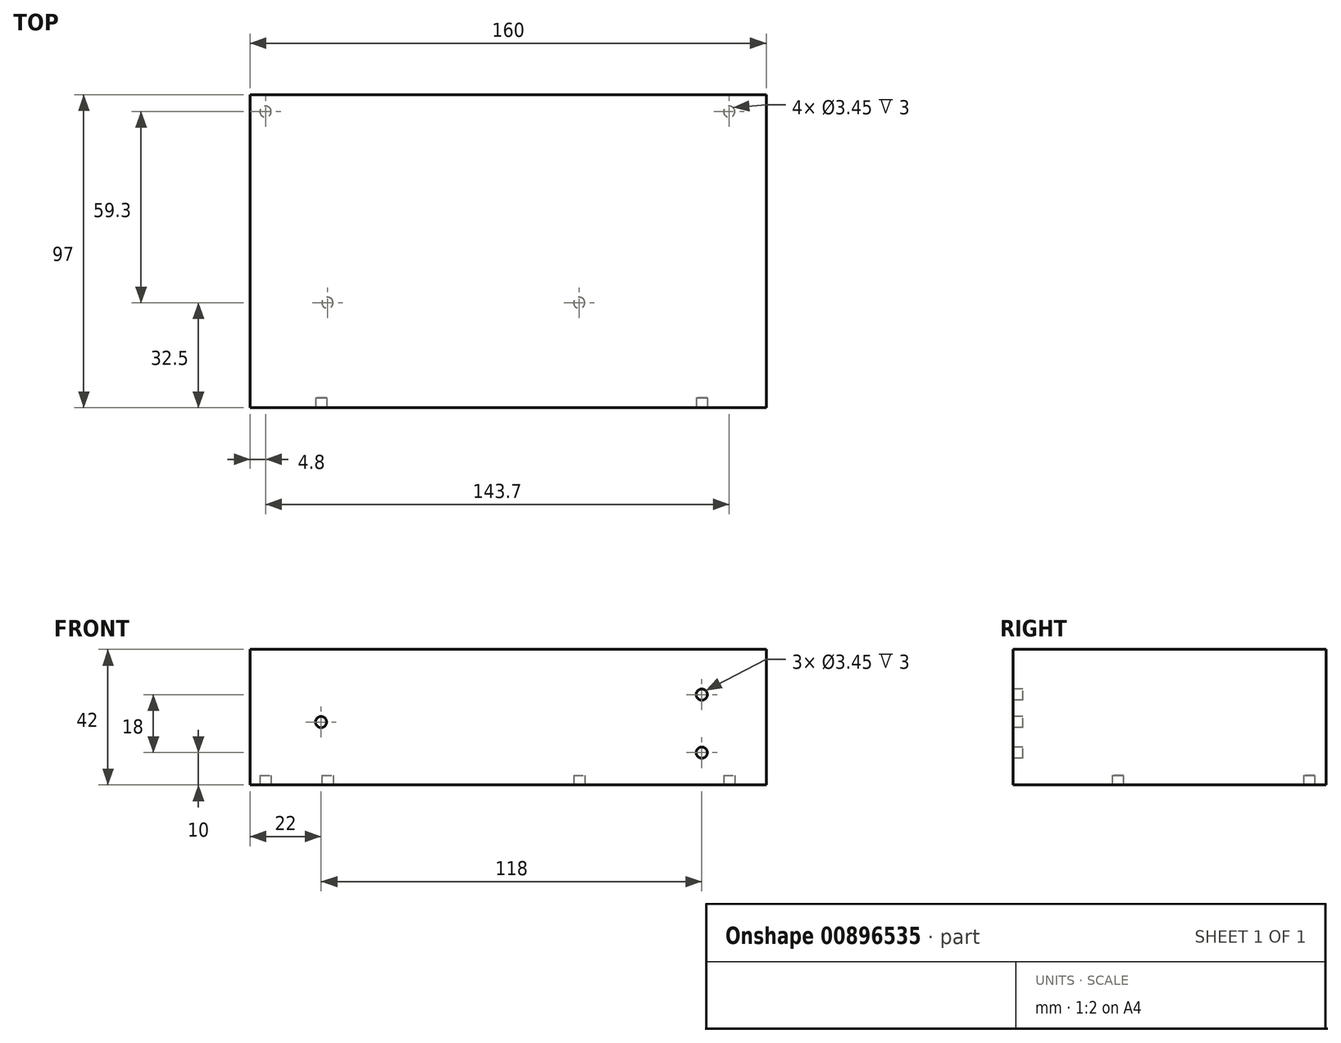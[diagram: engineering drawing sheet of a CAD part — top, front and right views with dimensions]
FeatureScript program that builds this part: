
annotation { "Feature Type Name" : "Feature", "Feature Type Description" : "" }
export const myFeature = defineFeature(function(context is Context, id is Id, definition is map)
    precondition{}
    {
        {
            var Q0;
            Q0=qCreatedBy(makeId("Top.planeOp"),FACE);
            var sketch = newSketch(context, id + "F0", { "sketchPlane" : qUnion([Q0])});
            skLineSegment(sketch, "E0.bottom", {"start": v(0, 0) * mm, "end": v(160, 0) * mm});
            skLineSegment(sketch, "E0.top", {"start": v(0, 97) * mm, "end": v(160, 97) * mm});
            skLineSegment(sketch, "E0.left", {"start": v(0, 0) * mm, "end": v(0, 97) * mm});
            skLineSegment(sketch, "E0.right", {"start": v(160, 0) * mm, "end": v(160, 97) * mm});
            skSolve(sketch);
        }
        {
            var Q0;
            Q0 = qSketchRegion(id + "F0", true);
            extrude(context, id + "F1", {"entities" : qUnion([Q0]), "depth" : 42 * mm, "offsetDistance" : 25 * mm});
        }
        {
            var Q0;
            Q0=makeQuery(id+"F1.opExtrude","SWEPT_FACE",FACE,{"disambiguationData":[OSD([sQuery(id+"F0.wireOp",EDGE,"E0.bottom")])]});
            var sketch = newSketch(context, id + "F2", { "sketchPlane" : qUnion([Q0])});
            skLineSegment(sketch, "E1", {"start": v(140, 0) * mm, "end": v(140, 10) * mm, "construction": true});
            skLineSegment(sketch, "E2", {"start": v(140, 10) * mm, "end": v(160, 10) * mm, "construction": true});
            skCircle(sketch, "E3", {"center": v(140, 10) * mm, "radius": 1.72 * mm});
            skLineSegment(sketch, "E4", {"start": v(140, 10) * mm, "end": v(140, 28) * mm, "construction": true});
            skCircle(sketch, "E5", {"center": v(140, 28) * mm, "radius": 1.72 * mm});
            skLineSegment(sketch, "E6", {"start": v(0, 19.5) * mm, "end": v(22, 19.5) * mm, "construction": true});
            skLineSegment(sketch, "E7", {"start": v(22, 19.5) * mm, "end": v(22, 0) * mm, "construction": true});
            skCircle(sketch, "E8", {"center": v(22, 19.5) * mm, "radius": 1.72 * mm});
            skSolve(sketch);
        }
        {
            var Q0;
            Q0 = qSketchRegion(id + "F2", true);
            extrude(context, id + "F3", {"entities" : qUnion([Q0]), "operationType" : NewBodyOperationType.REMOVE, "oppositeDirection" : true, "depth" : 3 * mm, "offsetDistance" : 25 * mm});
        }
        {
            var Q0;
            Q0=makeQuery(id+"F1.opExtrude","CAP_FACE",FACE,{"disambiguationData":[OSD([sQuery(id+"F0.wireOp",EDGE,"E0.bottom"),sQuery(id+"F0.wireOp",EDGE,"E0.top"),sQuery(id+"F0.wireOp",EDGE,"E0.left"),sQuery(id+"F0.wireOp",EDGE,"E0.right")])],"isStart":true});
            var sketch = newSketch(context, id + "F4", { "sketchPlane" : qUnion([Q0])});
            skLineSegment(sketch, "E9", {"start": v(0, -91.8) * mm, "end": v(4.8, -91.8) * mm, "construction": true});
            skLineSegment(sketch, "E10", {"start": v(4.8, -91.8) * mm, "end": v(4.8, -97) * mm, "construction": true});
            skCircle(sketch, "E11", {"center": v(4.8, -91.8) * mm, "radius": 1.73 * mm});
            skLineSegment(sketch, "E12", {"start": v(148.5, -97) * mm, "end": v(148.5, -91.8) * mm, "construction": true});
            skLineSegment(sketch, "E13", {"start": v(148.5, -91.8) * mm, "end": v(160, -91.8) * mm, "construction": true});
            skLineSegment(sketch, "E14", {"start": v(24, 0) * mm, "end": v(24, -32.5) * mm, "construction": true});
            skLineSegment(sketch, "E15", {"start": v(24, -32.5) * mm, "end": v(0, -32.5) * mm, "construction": true});
            skCircle(sketch, "E16", {"center": v(24, -32.5) * mm, "radius": 1.72 * mm});
            skCircle(sketch, "E17", {"center": v(148.5, -91.8) * mm, "radius": 1.72 * mm});
            skLineSegment(sketch, "E18", {"start": v(24, -32.5) * mm, "end": v(102, -32.5) * mm, "construction": true});
            skCircle(sketch, "E19", {"center": v(102, -32.5) * mm, "radius": 1.72 * mm});
            skSolve(sketch);
        }
        {
            var Q0;
            Q0 = qSketchRegion(id + "F4", true);
            extrude(context, id + "F5", {"entities" : qUnion([Q0]), "operationType" : NewBodyOperationType.REMOVE, "oppositeDirection" : true, "depth" : 3 * mm, "offsetDistance" : 25 * mm});
        }
    });
